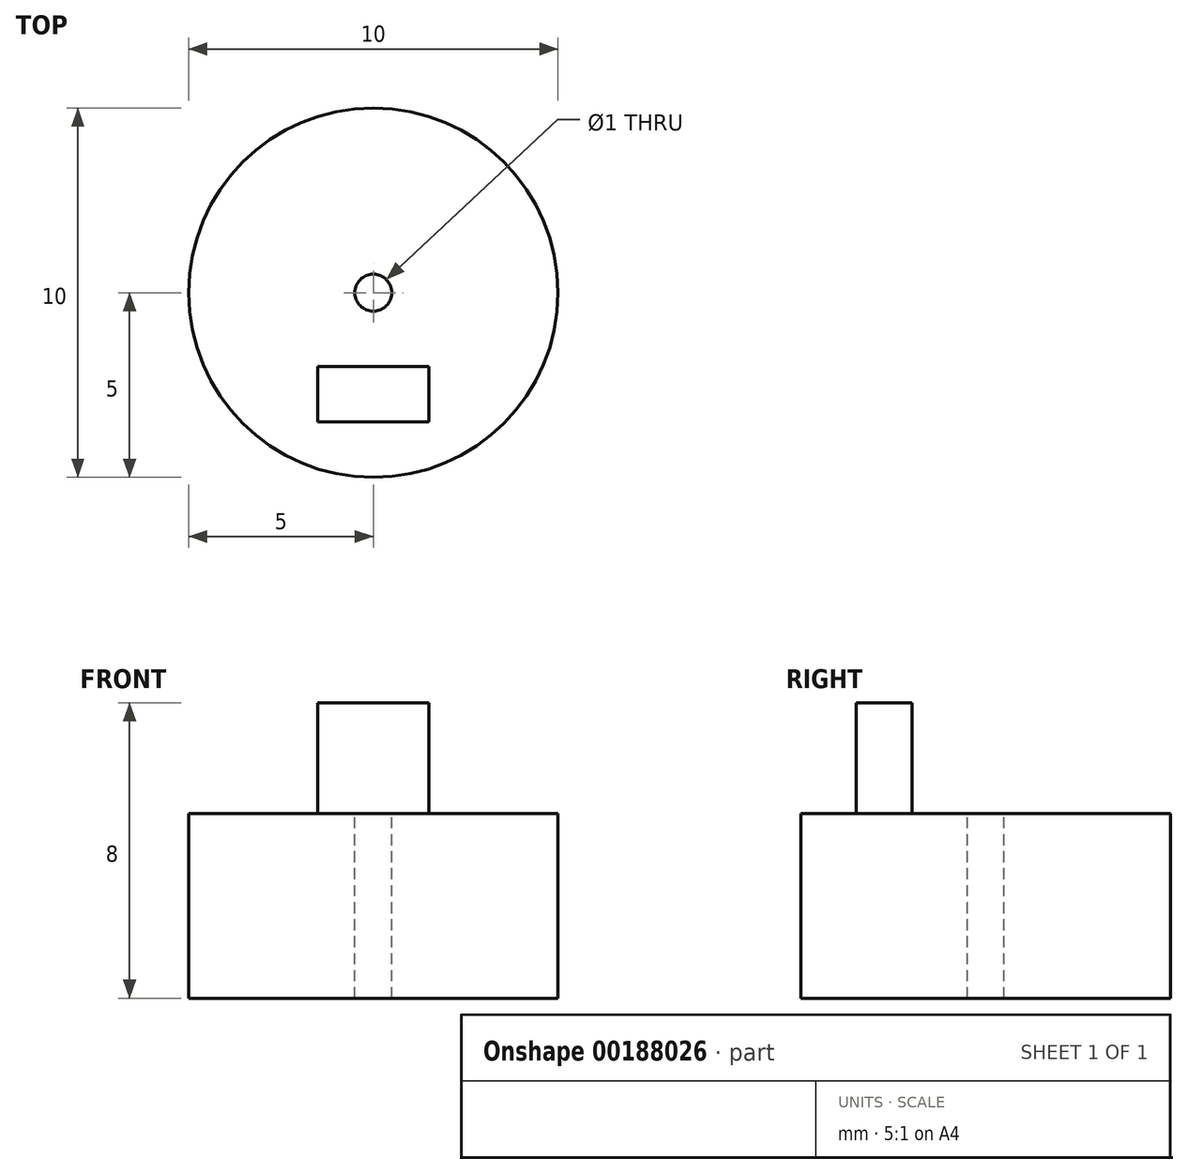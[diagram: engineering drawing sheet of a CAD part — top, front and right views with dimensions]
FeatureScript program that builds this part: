
annotation { "Feature Type Name" : "Feature", "Feature Type Description" : "" }
export const myFeature = defineFeature(function(context is Context, id is Id, definition is map)
    precondition{}
    {
        {
            var Q0;
            Q0=qCreatedBy(makeId("Top.planeOp"),FACE);
            var sketch = newSketch(context, id + "F0", { "sketchPlane" : qUnion([Q0])});
            skCircle(sketch, "E0", {"center": v(0, 0) * mm, "radius": 5 * mm});
            skSolve(sketch);
        }
        {
            var Q0;
            Q0 = qSketchRegion(id + "F0", true);
            extrude(context, id + "F1", {"entities" : qUnion([Q0]), "depth" : 5 * mm});
        }
        {
            var Q0;
            Q0=makeQuery(id+"F1.opExtrude","CAP_FACE",FACE,{"disambiguationData":[OSD([sQuery(id+"F0.wireOp",EDGE,"E0")])],"isStart":false});
            var sketch = newSketch(context, id + "F2", { "sketchPlane" : qUnion([Q0])});
            skLineSegment(sketch, "E1.bottom", {"start": v(-1.5, -2) * mm, "end": v(1.5, -2) * mm});
            skLineSegment(sketch, "E1.top", {"start": v(-1.5, -3.5) * mm, "end": v(1.5, -3.5) * mm});
            skLineSegment(sketch, "E1.left", {"start": v(-1.5, -2) * mm, "end": v(-1.5, -3.5) * mm});
            skLineSegment(sketch, "E1.right", {"start": v(1.5, -2) * mm, "end": v(1.5, -3.5) * mm});
            skSolve(sketch);
        }
        {
            var Q0;
            Q0 = qSketchRegion(id + "F2", true);
            extrude(context, id + "F3", {"entities" : qUnion([Q0]), "operationType" : NewBodyOperationType.ADD, "depth" : 3 * mm});
        }
        {
            var Q0;
            Q0=makeQuery(id+"F1.opExtrude","CAP_FACE",FACE,{"disambiguationData":[OSD([sQuery(id+"F0.wireOp",EDGE,"E0")])],"isStart":false});
            var sketch = newSketch(context, id + "F4", { "sketchPlane" : qUnion([Q0])});
            skCircle(sketch, "E2", {"center": v(0, 0) * mm, "radius": 0.5 * mm});
            skSolve(sketch);
        }
        {
            var Q0;
            Q0 = qSketchRegion(id + "F4", true);
            extrude(context, id + "F5", {"entities" : qUnion([Q0]), "operationType" : NewBodyOperationType.REMOVE, "oppositeDirection" : true, "depth" : 25 * mm});
        }
    });
